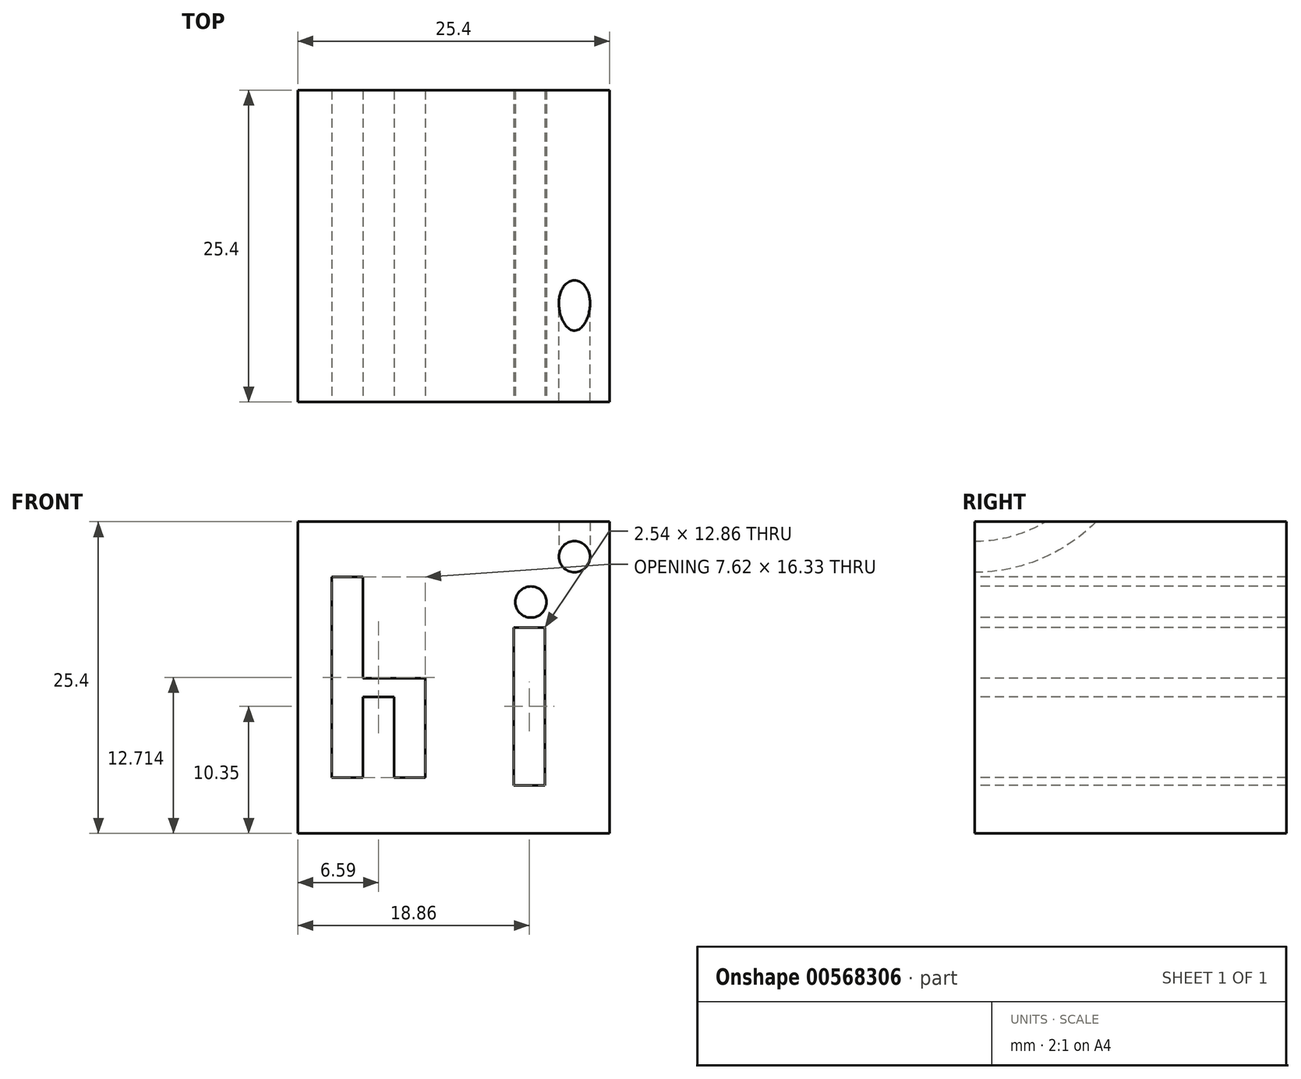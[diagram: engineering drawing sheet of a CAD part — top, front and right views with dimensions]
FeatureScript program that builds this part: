
annotation { "Feature Type Name" : "Feature", "Feature Type Description" : "" }
export const myFeature = defineFeature(function(context is Context, id is Id, definition is map)
    precondition{}
    {
        {
            var Q0;
            Q0=qCreatedBy(makeId("Front.planeOp"),FACE);
            var sketch = newSketch(context, id + "F0", { "sketchPlane" : qUnion([Q0])});
            skLineSegment(sketch, "E0.bottom", {"start": v(0, 0) * mm, "end": v(25.4, 0) * mm});
            skLineSegment(sketch, "E0.top", {"start": v(0, 25.4) * mm, "end": v(25.4, 25.4) * mm});
            skLineSegment(sketch, "E0.left", {"start": v(0, 0) * mm, "end": v(0, 25.4) * mm});
            skLineSegment(sketch, "E0.right", {"start": v(25.4, 0) * mm, "end": v(25.4, 25.4) * mm});
            skSolve(sketch);
        }
        {
            var Q0;
            Q0 = qSketchRegion(id + "F0", true);
            extrude(context, id + "F1", {"entities" : qUnion([Q0]), "depth" : 25.4 * mm, "offsetDistance" : 25.4 * mm});
        }
        {
            var Q0;
            Q0=makeQuery(id+"F1.opExtrude","CAP_FACE",FACE,{"disambiguationData":[OSD([sQuery(id+"F0.wireOp",EDGE,"E0.bottom"),sQuery(id+"F0.wireOp",EDGE,"E0.top"),sQuery(id+"F0.wireOp",EDGE,"E0.left"),sQuery(id+"F0.wireOp",EDGE,"E0.right")])],"isStart":false});
            var sketch = newSketch(context, id + "F2", { "sketchPlane" : qUnion([Q0])});
            skLineSegment(sketch, "E1", {"start": v(5.32, 12.66) * mm, "end": v(10.4, 12.66) * mm});
            skLineSegment(sketch, "E2", {"start": v(10.4, 12.66) * mm, "end": v(10.4, 4.55) * mm});
            skLineSegment(sketch, "E3", {"start": v(10.4, 4.55) * mm, "end": v(7.86, 4.55) * mm});
            skLineSegment(sketch, "E4", {"start": v(7.86, 4.55) * mm, "end": v(7.86, 11.11) * mm});
            skLineSegment(sketch, "E5", {"start": v(7.86, 11.11) * mm, "end": v(5.32, 11.11) * mm});
            skLineSegment(sketch, "E6", {"start": v(5.32, 11.11) * mm, "end": v(5.32, 4.55) * mm});
            skLineSegment(sketch, "E7", {"start": v(5.32, 4.55) * mm, "end": v(4.54, 4.55) * mm});
            skLineSegment(sketch, "E8", {"start": v(2.78, 4.55) * mm, "end": v(2.78, 20.88) * mm});
            skLineSegment(sketch, "E9", {"start": v(2.78, 20.88) * mm, "end": v(4.54, 20.88) * mm});
            skLineSegment(sketch, "E10", {"start": v(2.78, 4.55) * mm, "end": v(4.54, 4.55) * mm});
            skPoint(sketch, "E11.start.orphan", {"position": v(4.54, 20.76) * mm});
            skLineSegment(sketch, "E12", {"start": v(4.54, 20.88) * mm, "end": v(5.32, 20.88) * mm});
            skLineSegment(sketch, "E13", {"start": v(5.32, 20.88) * mm, "end": v(5.32, 12.66) * mm});
            skPoint(sketch, "E14.orphan", {"position": v(4.54, 12.66) * mm});
            skLineSegment(sketch, "E15", {"start": v(17.6, 16.77) * mm, "end": v(17.6, 3.92) * mm});
            skPoint(sketch, "E15.startSnap0", {"position": v(5.32, 16.77) * mm});
            skLineSegment(sketch, "E16", {"start": v(17.6, 3.92) * mm, "end": v(20.13, 3.92) * mm});
            skLineSegment(sketch, "E17", {"start": v(20.13, 3.92) * mm, "end": v(20.13, 16.78) * mm});
            skLineSegment(sketch, "E18", {"start": v(20.13, 16.78) * mm, "end": v(17.6, 16.77) * mm});
            skCircle(sketch, "E19", {"center": v(19, 18.85) * mm, "radius": 1.27 * mm});
            skSolve(sketch);
        }
        {
            var Q0;
            Q0=makeQuery(id+"F2.imprint","IMPRINT",FACE,{"disambiguationData":[TD([[makeQuery(id+"F2.imprint","IMPRINT",EDGE,{"derivedFrom":sQuery(id+"F2.wireOp",EDGE,"E1")}),-1.0]])]});
            var Q1;
            Q1=makeQuery(id+"F2.imprint","IMPRINT",FACE,{"disambiguationData":[TD([[makeQuery(id+"F2.imprint","IMPRINT",EDGE,{"derivedFrom":sQuery(id+"F2.wireOp",EDGE,"E15")}),1.0]])]});
            var Q2;
            Q2=makeQuery(id+"F2.imprint","IMPRINT",FACE,{"disambiguationData":[TD([[makeQuery(id+"F2.imprint","IMPRINT",EDGE,{"derivedFrom":sQuery(id+"F2.wireOp",EDGE,"E19")}),1.0]])]});
            extrude(context, id + "F3", {"entities" : qUnion([Q0, Q1, Q2]), "operationType" : NewBodyOperationType.REMOVE, "oppositeDirection" : true, "depth" : 25.4 * mm, "offsetDistance" : 25.4 * mm});
        }
        {
            var Q0;
            Q0=makeQuery(id+"F1.opExtrude","CAP_FACE",FACE,{"disambiguationData":[OSD([sQuery(id+"F0.wireOp",EDGE,"E0.bottom"),sQuery(id+"F0.wireOp",EDGE,"E0.top"),sQuery(id+"F0.wireOp",EDGE,"E0.left"),sQuery(id+"F0.wireOp",EDGE,"E0.right")])],"isStart":false});
            var sketch = newSketch(context, id + "F4", { "sketchPlane" : qUnion([Q0])});
            skCircle(sketch, "E20", {"center": v(22.54, 22.54) * mm, "radius": 1.27 * mm});
            skLineSegment(sketch, "E21", {"start": v(18.05, 35.24) * mm, "end": v(29.02, 35.24) * mm});
            skSolve(sketch);
        }
        {
            var Q0;
            Q0 = qSketchRegion(id + "F4", true);
            var Q1;
            Q1=sQuery(id+"F4.wireOp",EDGE,"E21");
            revolve(context, id + "F5", {"operationType" : NewBodyOperationType.REMOVE, "entities" : qUnion([Q0]), "axis" : qUnion([Q1]), "revolveType" : RevolveType.FULL});
        }
    });
